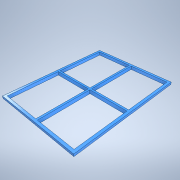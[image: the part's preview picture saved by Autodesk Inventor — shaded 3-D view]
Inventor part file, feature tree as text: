
AUTODESK INVENTOR PART (.ipt)
format: ipt  version: 2021 (Build 250183000, 183)  size: 169,472 bytes
history: native  units: mm
features: extrude x3, sketch x3
ambient origin geometry x8: Origin, YZ Plane, XZ Plane, XY Plane, X Axis, Y Axis, Z Axis, Center Point
bodies: Solid1 (feature_tree)
feature tree (6):
  extrude  "Extrusion1"  Depth=140.0mm
  extrude  "Extrusion4"  Depth=105.0mm
  extrude  "Extrusion5"  Depth=140.0mm
  sketch  "Sketch4"  dims[d78=20.0mm d79=-5.235988mm d84=140.0mm]
  sketch  "Sketch10"  dims[d85=105.0mm d107=44.5mm]
  sketch  "Sketch11"  dims[d108=62.0mm d118=140.0mm d119=90.0deg d120=0.0mm d121=0.0mm d123=5.0mm d124=5.0mm d125=20.0mm d127=68.0mm d128=20.0mm d130=50.5mm d133=3.0mm d134=0.0mm d82=0.5mm d83=0.872665mm d86=0.5mm d87=0.872665mm]
